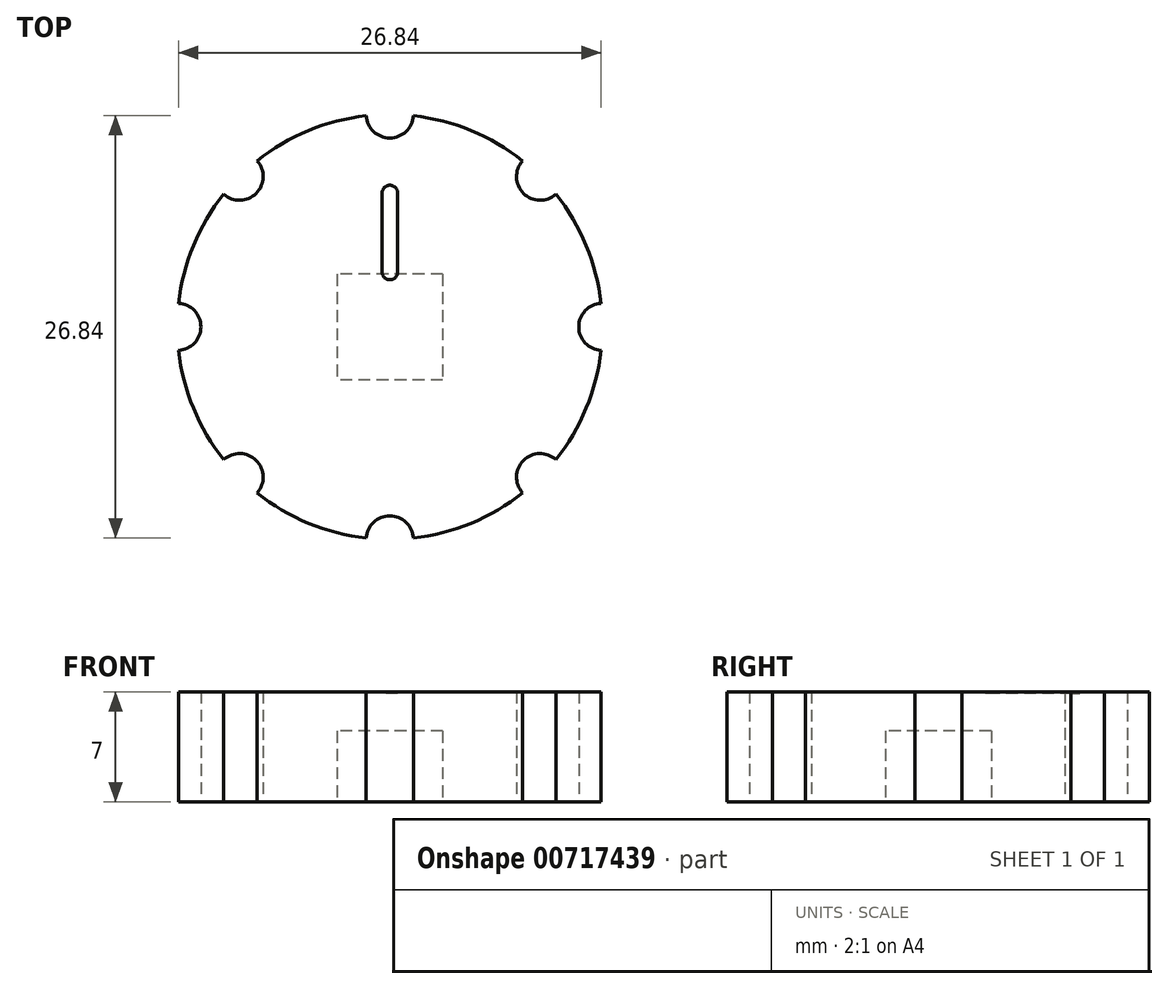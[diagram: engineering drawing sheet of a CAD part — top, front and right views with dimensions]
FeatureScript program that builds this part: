
annotation { "Feature Type Name" : "Feature", "Feature Type Description" : "" }
export const myFeature = defineFeature(function(context is Context, id is Id, definition is map)
    precondition{}
    {
        {
            var Q0;
            Q0=qCreatedBy(makeId("Top.planeOp"),FACE);
            var sketch = newSketch(context, id + "F0", { "sketchPlane" : qUnion([Q0])});
            skCircle(sketch, "E0", {"center": v(0, 0) * mm, "radius": 13.5 * mm});
            skSolve(sketch);
        }
        {
            var Q0;
            Q0 = qSketchRegion(id + "F0", true);
            extrude(context, id + "F1", {"entities" : qUnion([Q0]), "depth" : 7 * mm, "offsetDistance" : 25.4 * mm});
        }
        {
            var Q0;
            Q0=qCreatedBy(makeId("Top.planeOp"),FACE);
            var sketch = newSketch(context, id + "F2", { "sketchPlane" : qUnion([Q0])});
            skLineSegment(sketch, "E1.bottom", {"start": v(3.36, 3.36) * mm, "end": v(-3.36, 3.36) * mm});
            skLineSegment(sketch, "E1.top", {"start": v(3.36, -3.36) * mm, "end": v(-3.36, -3.36) * mm});
            skLineSegment(sketch, "E1.left", {"start": v(3.36, 3.36) * mm, "end": v(3.36, -3.36) * mm});
            skLineSegment(sketch, "E1.right", {"start": v(-3.36, 3.36) * mm, "end": v(-3.36, -3.36) * mm});
            skPoint(sketch, "E1.middle", {"position": v(0, 0) * mm});
            skSolve(sketch);
        }
        {
            var Q0;
            Q0 = qSketchRegion(id + "F2", true);
            extrude(context, id + "F3", {"entities" : qUnion([Q0]), "operationType" : NewBodyOperationType.REMOVE, "depth" : 4.5 * mm, "offsetDistance" : 25.4 * mm});
        }
        {
            var Q0;
            Q0=qCreatedBy(makeId("Top.planeOp"),FACE);
            var sketch = newSketch(context, id + "F4", { "sketchPlane" : qUnion([Q0])});
            skCircle(sketch, "E2", {"center": v(13.5, 0) * mm, "radius": 1.5 * mm});
            skCircle(sketch, "E3", {"center": v(-13.5, 0) * mm, "radius": 1.5 * mm});
            skCircle(sketch, "E4", {"center": v(0, -13.5) * mm, "radius": 1.5 * mm});
            skCircle(sketch, "E5.MirrorC", {"center": v(0, 13.5) * mm, "radius": 1.5 * mm});
            skLineSegment(sketch, "E6", {"start": v(-13.5, 13.5) * mm, "end": v(13.5, -13.5) * mm});
            skLineSegment(sketch, "E7.MirrorCS", {"start": v(13.5, 13.5) * mm, "end": v(-13.5, -13.5) * mm});
            skCircle(sketch, "E8", {"center": v(-9.55, -9.55) * mm, "radius": 1.5 * mm});
            skCircle(sketch, "E9.MirrorC", {"center": v(9.55, 9.55) * mm, "radius": 1.5 * mm});
            skCircle(sketch, "E10", {"center": v(9.55, -9.55) * mm, "radius": 1.5 * mm});
            skCircle(sketch, "E11.MirrorC", {"center": v(-9.55, 9.55) * mm, "radius": 1.5 * mm});
            skSolve(sketch);
        }
        {
            var Q0;
            Q0 = qSketchRegion(id + "F4", true);
            extrude(context, id + "F5", {"entities" : qUnion([Q0]), "operationType" : NewBodyOperationType.REMOVE, "depth" : 25.4 * mm, "offsetDistance" : 25.4 * mm});
        }
        {
            var Q0;
            Q0=qCreatedBy(makeId("Top.planeOp"),FACE);
            cPlane(context, id + "F6", {"entities" : qUnion([Q0]), "cplaneType" : CPlaneType.OFFSET, "offset" : 7 * mm, "width" : 152.4 * mm, "height" : 152.4 * mm});
        }
        {
            var Q0;
            Q0=qCreatedBy(id+"F6.planeOp",FACE);
            var sketch = newSketch(context, id + "F7", { "sketchPlane" : qUnion([Q0])});
            skLineSegment(sketch, "E12.bottom", {"start": v(0.5, 8.5) * mm, "end": v(-0.5, 8.5) * mm});
            skLineSegment(sketch, "E12.top", {"start": v(0.5, 3.5) * mm, "end": v(-0.5, 3.5) * mm});
            skLineSegment(sketch, "E12.left", {"start": v(0.5, 8.5) * mm, "end": v(0.5, 3.5) * mm});
            skLineSegment(sketch, "E12.right", {"start": v(-0.5, 8.5) * mm, "end": v(-0.5, 3.5) * mm});
            skPoint(sketch, "E12.middle", {"position": v(0, 6) * mm});
            skCircle(sketch, "E13", {"center": v(0, 8.5) * mm, "radius": 0.5 * mm});
            skCircle(sketch, "E14", {"center": v(0, 3.5) * mm, "radius": 0.5 * mm});
            skSolve(sketch);
        }
        {
            var Q0;
            Q0 = qSketchRegion(id + "F7", true);
            extrude(context, id + "F8", {"entities" : qUnion([Q0]), "operationType" : NewBodyOperationType.REMOVE, "oppositeDirection" : true, "depth" : 0.1 * mm, "offsetDistance" : 25.4 * mm});
        }
    });
